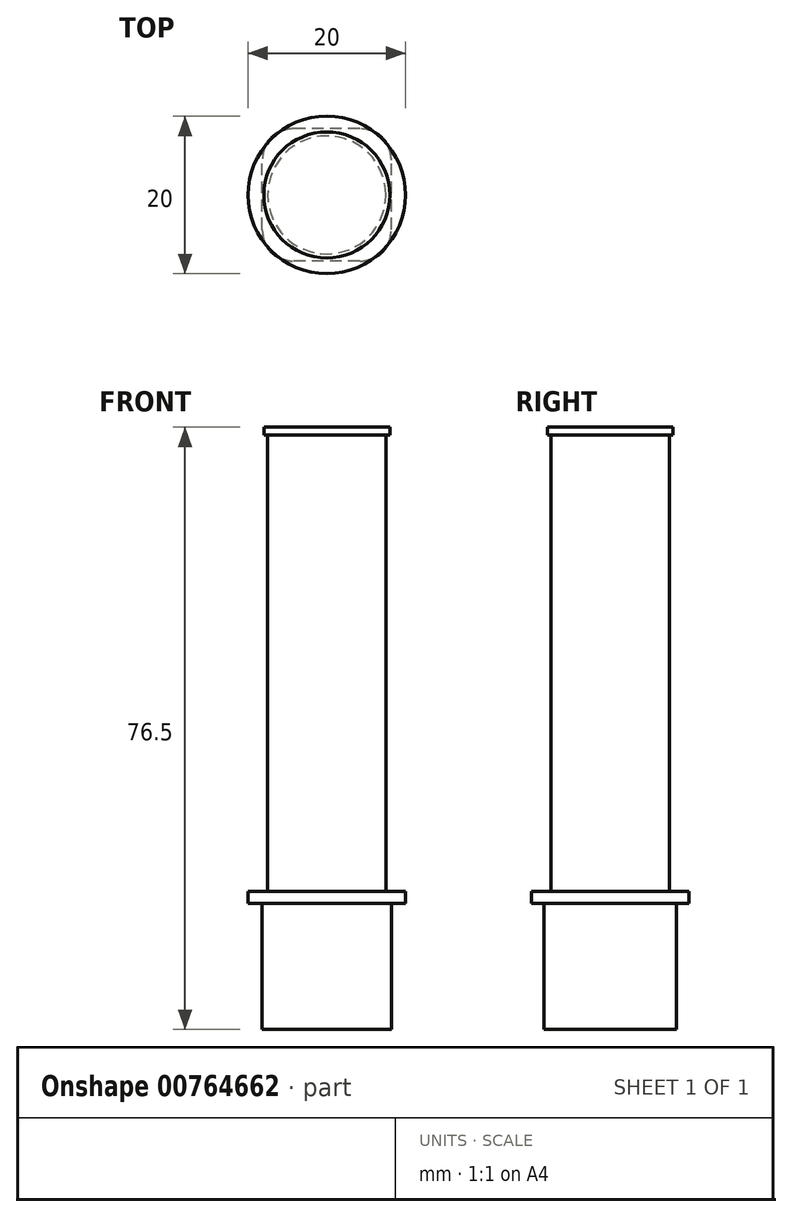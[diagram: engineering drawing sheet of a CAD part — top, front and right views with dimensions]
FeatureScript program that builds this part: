
annotation { "Feature Type Name" : "Feature", "Feature Type Description" : "" }
export const myFeature = defineFeature(function(context is Context, id is Id, definition is map)
    precondition{}
    {
        {
            var Q0;
            Q0=qCreatedBy(makeId("Top.planeOp"),FACE);
            var sketch = newSketch(context, id + "F0", { "sketchPlane" : qUnion([Q0])});
            skLineSegment(sketch, "E0.bottom", {"start": v(4.2, -8.4) * mm, "end": v(-4.2, -8.4) * mm});
            skLineSegment(sketch, "E0.top", {"start": v(4.2, 8.4) * mm, "end": v(-4.2, 8.4) * mm});
            skLineSegment(sketch, "E0.left", {"start": v(8.2, -4.4) * mm, "end": v(8.2, 4.4) * mm});
            skLineSegment(sketch, "E0.right", {"start": v(-8.2, -4.4) * mm, "end": v(-8.2, 4.4) * mm});
            skPoint(sketch, "E0.middle", {"position": v(0, 0) * mm});
            skPoint(sketch, "E1.visualSharp", {"position": v(-8.2, 8.4) * mm});
            skArc(sketch, "E1.filletArc", {"start": v(-4.2, 8.4) * mm, "mid": v(-7.03, 7.23) * mm, "end": v(-8.2, 4.4) * mm});
            skPoint(sketch, "E2.visualSharp", {"position": v(8.2, 8.4) * mm});
            skArc(sketch, "E2.filletArc", {"start": v(8.2, 4.4) * mm, "mid": v(7.03, 7.23) * mm, "end": v(4.2, 8.4) * mm});
            skPoint(sketch, "E3.visualSharp", {"position": v(8.2, -8.4) * mm});
            skArc(sketch, "E3.filletArc", {"start": v(4.2, -8.4) * mm, "mid": v(7.03, -7.23) * mm, "end": v(8.2, -4.4) * mm});
            skPoint(sketch, "E4.visualSharp", {"position": v(-8.2, -8.4) * mm});
            skArc(sketch, "E4.filletArc", {"start": v(-8.2, -4.4) * mm, "mid": v(-7.03, -7.23) * mm, "end": v(-4.2, -8.4) * mm});
            skSolve(sketch);
        }
        {
            var Q0;
            Q0 = qSketchRegion(id + "F0", true);
            extrude(context, id + "F1", {"entities" : qUnion([Q0]), "oppositeDirection" : true, "depth" : 16 * mm, "offsetDistance" : 25 * mm});
        }
        {
            var Q0;
            Q0=qCreatedBy(makeId("Right.planeOp"),FACE);
            var sketch = newSketch(context, id + "F2", { "sketchPlane" : qUnion([Q0])});
            skLineSegment(sketch, "E5.bottom", {"start": v(0, 0) * mm, "end": v(-10, 0) * mm});
            skLineSegment(sketch, "E5.top", {"start": v(0, 1.5) * mm, "end": v(-10, 1.5) * mm});
            skLineSegment(sketch, "E5.left", {"start": v(0, 0) * mm, "end": v(0, 1.5) * mm});
            skLineSegment(sketch, "E5.right", {"start": v(-10, 0) * mm, "end": v(-10, 1.5) * mm});
            skLineSegment(sketch, "E6.bottom", {"start": v(0, 1.5) * mm, "end": v(-7.5, 1.5) * mm});
            skLineSegment(sketch, "E6.top", {"start": v(0, 59.5) * mm, "end": v(-7.5, 59.5) * mm});
            skLineSegment(sketch, "E6.left", {"start": v(0, 1.5) * mm, "end": v(0, 59.5) * mm});
            skLineSegment(sketch, "E6.right", {"start": v(-7.5, 1.5) * mm, "end": v(-7.5, 59.5) * mm});
            skLineSegment(sketch, "E7.bottom", {"start": v(0, 59.5) * mm, "end": v(-8, 59.5) * mm});
            skLineSegment(sketch, "E7.top", {"start": v(0, 60.5) * mm, "end": v(-8, 60.5) * mm});
            skLineSegment(sketch, "E7.left", {"start": v(0, 59.5) * mm, "end": v(0, 60.5) * mm});
            skLineSegment(sketch, "E7.right", {"start": v(-8, 59.5) * mm, "end": v(-8, 60.5) * mm});
            skSolve(sketch);
        }
        {
            var Q0;
            Q0 = qSketchRegion(id + "F2", true);
            var Q1;
            Q1=sQuery(id+"F2.wireOp",EDGE,"E6.left");
            revolve(context, id + "F3", {"operationType" : NewBodyOperationType.ADD, "surfaceOperationType" : NewSurfaceOperationType.NEW, "entities" : qUnion([Q0]), "axis" : qUnion([Q1]), "revolveType" : RevolveType.FULL});
        }
    });
